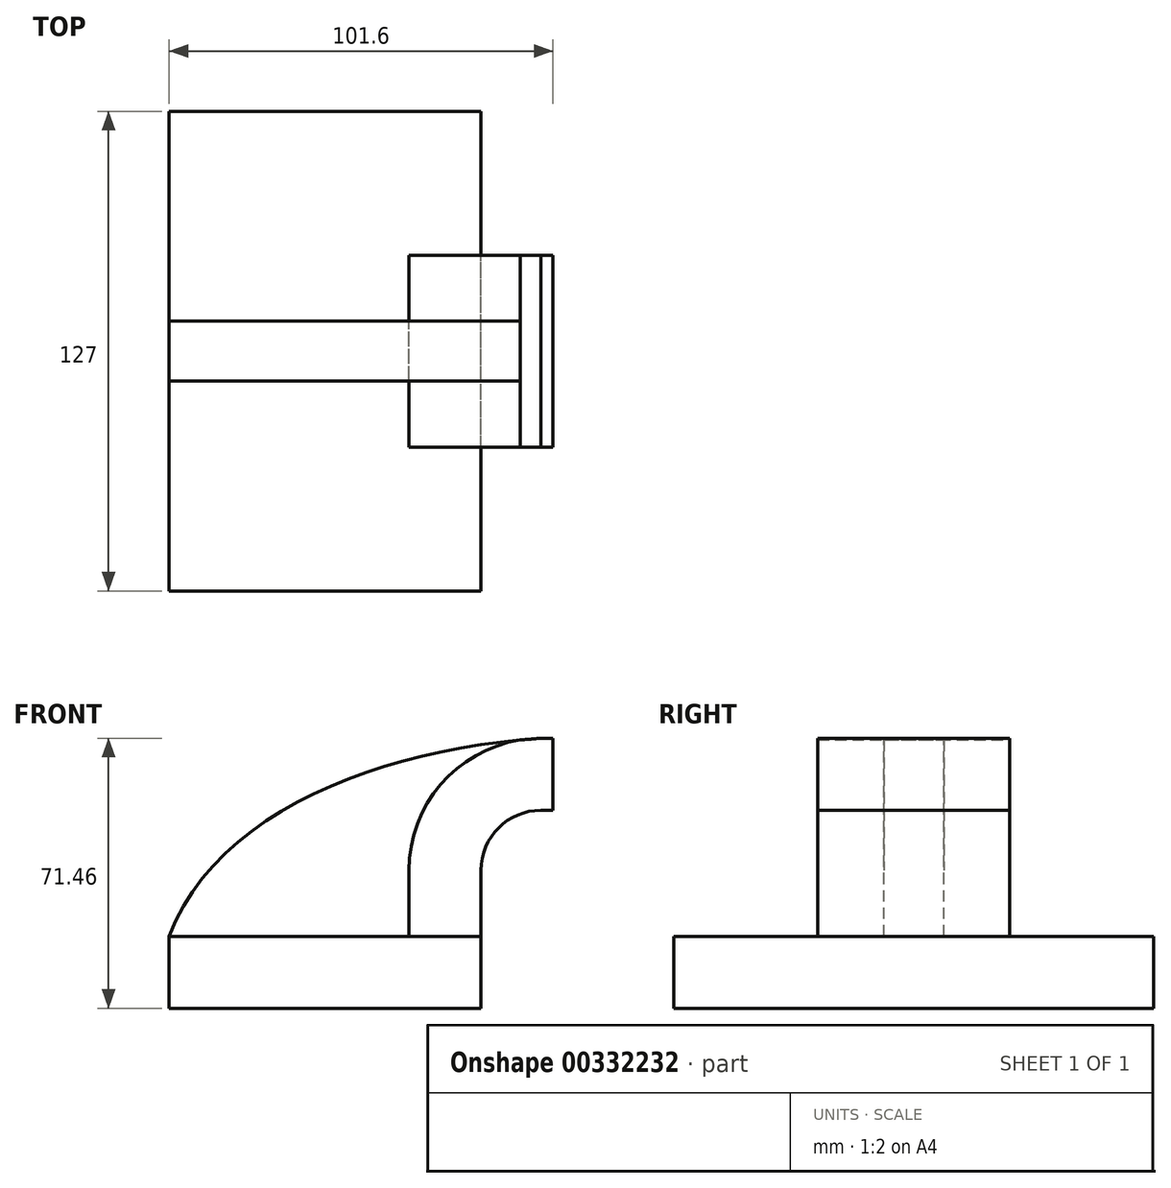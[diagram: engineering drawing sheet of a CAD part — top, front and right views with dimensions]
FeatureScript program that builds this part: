
annotation { "Feature Type Name" : "Feature", "Feature Type Description" : "" }
export const myFeature = defineFeature(function(context is Context, id is Id, definition is map)
    precondition{}
    {
        {
            var Q0;
            Q0=qCreatedBy(makeId("Front.planeOp"),FACE);
            var sketch = newSketch(context, id + "F0", { "sketchPlane" : qUnion([Q0])});
            skLineSegment(sketch, "E0.bottom", {"start": v(-41.28, 9.52) * mm, "end": v(41.28, 9.53) * mm});
            skLineSegment(sketch, "E0.top", {"start": v(-41.28, -9.53) * mm, "end": v(41.28, -9.53) * mm});
            skLineSegment(sketch, "E0.left", {"start": v(-41.28, 9.52) * mm, "end": v(-41.28, -9.53) * mm});
            skLineSegment(sketch, "E0.right", {"start": v(41.28, 9.53) * mm, "end": v(41.28, -9.52) * mm});
            skPoint(sketch, "E0.middle", {"position": v(0, 0) * mm});
            skLineSegment(sketch, "E1.bottom", {"start": v(111.12, 38.1) * mm, "end": v(60.32, 38.1) * mm});
            skLineSegment(sketch, "E1.top", {"start": v(111.12, 66.68) * mm, "end": v(60.32, 66.68) * mm});
            skLineSegment(sketch, "E1.left", {"start": v(111.12, 38.1) * mm, "end": v(111.12, 66.68) * mm});
            skLineSegment(sketch, "E1.right", {"start": v(60.32, 38.1) * mm, "end": v(60.32, 66.68) * mm});
            skPoint(sketch, "E1.middle", {"position": v(85.72, 52.39) * mm});
            skLineSegment(sketch, "E2", {"start": v(41.27, 9.53) * mm, "end": v(41.27, 27) * mm});
            skArc(sketch, "E3", {"start": v(41.27, 27) * mm, "mid": v(45.92, 38.23) * mm, "end": v(57.15, 42.88) * mm});
            skLineSegment(sketch, "E4", {"start": v(57.15, 42.88) * mm, "end": v(85.5, 42.88) * mm});
            skLineSegment(sketch, "E5.0", {"start": v(57.15, 61.93) * mm, "end": v(85.5, 61.93) * mm});
            skArc(sketch, "E5.1", {"start": v(22.22, 27) * mm, "mid": v(32.45, 51.7) * mm, "end": v(57.15, 61.93) * mm});
            skLineSegment(sketch, "E5.2", {"start": v(22.23, 9.53) * mm, "end": v(22.23, 27) * mm});
            skLineSegment(sketch, "E6", {"start": v(85.5, 61.93) * mm, "end": v(85.5, 42.88) * mm});
            skFitSpline(sketch, "E7", {"points": [v(-41.28, 9.53) * mm, v(57.15, 61.93) * mm], "startDerivative": vector(37.76, 100.4) * mm, "endDerivative": vector(124.67, 8.09) * mm});
            skSolve(sketch);
        }
        {
            var Q0;
            Q0=makeQuery(id+"F0.imprint","IMPRINT",FACE,{"disambiguationData":[TD([[makeQuery(id+"F0.imprint","IMPRINT",EDGE,{"derivedFrom":sQuery(id+"F0.wireOp",EDGE,"E0.top")}),1.0]])]});
            extrude(context, id + "F1", {"entities" : qUnion([Q0]), "endBound" : BoundingType.SYMMETRIC, "depth" : 127 * mm});
        }
        {
            var Q0;
            {var subQ1=sQuery(id+"F0.wireOp",EDGE,"E2");Q0=makeQuery(id+"F0.imprint","IMPRINT",FACE,{"disambiguationData":[TD([[makeQuery(id+"F0.imprint","IMPRINT",EDGE,{"derivedFrom":subQ1}),1.0]])]});}
            extrude(context, id + "F2", {"entities" : qUnion([Q0]), "endBound" : BoundingType.SYMMETRIC, "depth" : 50.8 * mm});
        }
        {
            var Q0;
            {var subQ3=sQuery(id+"F0.wireOp",EDGE,"E5.2");Q0=makeQuery(id+"F0.imprint","IMPRINT",FACE,{"disambiguationData":[TD([[makeQuery(id+"F0.imprint","IMPRINT",EDGE,{"derivedFrom":subQ3}),1.0]])]});}
            extrude(context, id + "F3", {"entities" : qUnion([Q0]), "endBound" : BoundingType.SYMMETRIC, "depth" : 15.88 * mm});
        }
    });
